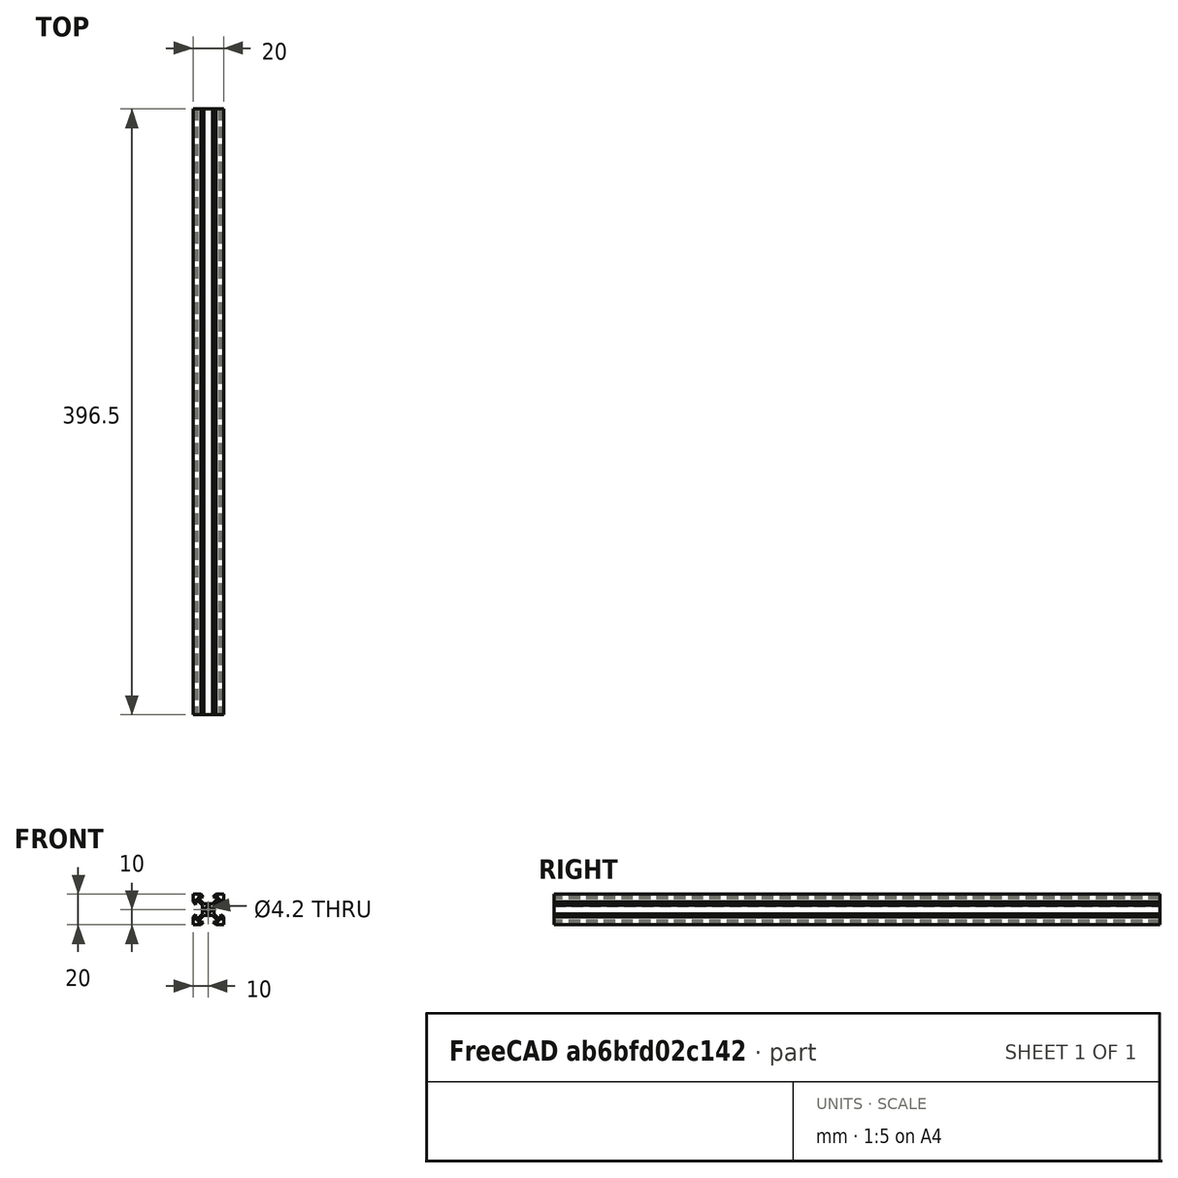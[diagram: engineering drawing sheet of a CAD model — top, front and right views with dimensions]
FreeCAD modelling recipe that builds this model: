
FCSTD DOCUMENT  (FreeCAD 0.20R29177 (Git))
Label: Vlot short
License: All rights reserved
LicenseURL: http://en.wikipedia.org/wiki/All_rights_reserved
objects: Sketcher::SketchObject×1, PartDesign::Pad×1, PartDesign::Body×1
note: 4 computed .brp shape members not serialized (recipe doc carries the construction recipe); baked Part::Feature solids carry a one-line shape summary decoded from their .brp

FEATURE [Sketcher::SketchObject] Sketch
  FullyConstrained = true
  MapMode = 5
  Placement = pos=(0,0,0) rot=(1,0,0;1.5708rad)
  Support = -> [XZ_Plane]
  sketch-geometry (43):
    g0: LineSegment StartX=0 StartY=0 StartZ=0 EndX=5.05 EndY=0 EndZ=0
    g1: LineSegment StartX=20 StartY=20 StartZ=0 EndX=14.95 EndY=20 EndZ=0
    g2: LineSegment StartX=0 StartY=20 StartZ=0 EndX=0 EndY=14.95 EndZ=0
    g3: LineSegment StartX=5.05 StartY=20 StartZ=0 EndX=6.9 EndY=18.15 EndZ=0
    g4: LineSegment StartX=6.9 StartY=18.15 StartZ=0 EndX=2.91066 EndY=18.15 EndZ=0
    g5: LineSegment StartX=2.91066 StartY=18.15 StartZ=0 EndX=7.16066 EndY=13.9 EndZ=0
    g6: LineSegment StartX=7.16066 StartY=13.9 StartZ=0 EndX=12.8393 EndY=13.9 EndZ=0
    g7: LineSegment StartX=12.8393 StartY=13.9 StartZ=0 EndX=17.0893 EndY=18.15 EndZ=0
    g8: LineSegment StartX=17.0893 StartY=18.15 StartZ=0 EndX=13.1 EndY=18.15 EndZ=0
    g9: LineSegment StartX=13.1 StartY=18.15 StartZ=0 EndX=14.95 EndY=20 EndZ=0
    g10: LineSegment StartX=0 StartY=20 StartZ=0 EndX=2.91066 EndY=18.15 EndZ=0
    g11: LineSegment StartX=17.0893 StartY=18.15 StartZ=0 EndX=20 EndY=20 EndZ=0
    g12: LineSegment StartX=0 StartY=20 StartZ=0 EndX=20 EndY=0 EndZ=0
    g13: LineSegment StartX=5.05 StartY=20 StartZ=0 EndX=0 EndY=20 EndZ=0
    g14: LineSegment StartX=0 StartY=20 StartZ=0 EndX=20 EndY=20 EndZ=0
    g15: LineSegment StartX=20 StartY=14.95 StartZ=0 EndX=18.15 EndY=13.1 EndZ=0
    g16: LineSegment StartX=18.15 StartY=13.1 StartZ=0 EndX=18.15 EndY=17.0893 EndZ=0
    g17: LineSegment StartX=18.15 StartY=17.0893 StartZ=0 EndX=13.9 EndY=12.8393 EndZ=0
    g18: LineSegment StartX=13.9 StartY=12.8393 StartZ=0 EndX=13.9 EndY=7.16066 EndZ=0
    g19: LineSegment StartX=13.9 StartY=7.16066 StartZ=0 EndX=18.15 EndY=2.91066 EndZ=0
    g20: LineSegment StartX=20 StartY=14.95 StartZ=0 EndX=20 EndY=20 EndZ=0
    g21: LineSegment StartX=18.15 StartY=2.91066 StartZ=0 EndX=18.15 EndY=6.9 EndZ=0
    g22: LineSegment StartX=18.15 StartY=6.9 StartZ=0 EndX=20 EndY=5.05 EndZ=0
    g23: LineSegment StartX=20 StartY=5.05 StartZ=0 EndX=20 EndY=0 EndZ=0
    g24: LineSegment StartX=5.05 StartY=0 StartZ=0 EndX=6.9 EndY=1.85 EndZ=0
    g25: LineSegment StartX=6.9 StartY=1.85 StartZ=0 EndX=2.91066 EndY=1.85 EndZ=0
    g26: LineSegment StartX=2.91066 StartY=1.85 StartZ=0 EndX=7.16066 EndY=6.1 EndZ=0
    g27: LineSegment StartX=7.16066 StartY=6.1 StartZ=0 EndX=12.8393 EndY=6.1 EndZ=0
    g28: LineSegment StartX=12.8393 StartY=6.1 StartZ=0 EndX=17.0893 EndY=1.85 EndZ=0
    g29: LineSegment StartX=17.0893 StartY=1.85 StartZ=0 EndX=13.1 EndY=1.85 EndZ=0
    g30: LineSegment StartX=13.1 StartY=1.85 StartZ=0 EndX=14.95 EndY=0 EndZ=0
    g31: LineSegment StartX=14.95 StartY=0 StartZ=0 EndX=20 EndY=0 EndZ=0
    g32: LineSegment StartX=0 StartY=14.95 StartZ=0 EndX=1.85 EndY=13.1 EndZ=0
    g33: LineSegment StartX=1.85 StartY=13.1 StartZ=0 EndX=1.85 EndY=17.0893 EndZ=0
    g34: LineSegment StartX=1.85 StartY=17.0893 StartZ=0 EndX=6.1 EndY=12.8393 EndZ=0
    g35: LineSegment StartX=6.1 StartY=12.8393 StartZ=0 EndX=6.1 EndY=7.16066 EndZ=0
    g36: LineSegment StartX=6.1 StartY=7.16066 StartZ=0 EndX=1.85 EndY=2.91066 EndZ=0
    g37: LineSegment StartX=1.85 StartY=2.91066 StartZ=0 EndX=1.85 EndY=6.9 EndZ=0
    g38: LineSegment StartX=1.85 StartY=6.9 StartZ=0 EndX=-2e-16 EndY=5.05 EndZ=0
    g39: LineSegment StartX=-2e-16 StartY=5.05 StartZ=0 EndX=0 EndY=0 EndZ=0
    g40: LineSegment StartX=0 StartY=20 StartZ=0 EndX=0 EndY=0 EndZ=0
    g41: LineSegment StartX=0 StartY=0 StartZ=0 EndX=10 EndY=10 EndZ=0
    g42: Circle CenterX=10 CenterY=10 CenterZ=0 NormalX=0 NormalY=0 NormalZ=1 AngleXU=0 Radius=2.1
  constraints (119):
    c: Coincident(g20,g1)
    c: Coincident(g13,g2)
    c: Coincident(g39,g0)
    c: Horizontal(g0)
    c: Horizontal(g1)
    c: Vertical(g2)
    c: Coincident(g0,g-1)
    c: DistanceY(g39,g2) = 20
    c: Coincident(g4,g3)
    c: Horizontal(g4)
    c: Coincident(g6,g5)
    c: Horizontal(g6)
    c: Coincident(g8,g7)
    c: Horizontal(g8)
    c: Coincident(g9,g8)
    c: Equal(g3,g9)
    c: Equal(g8,g4)
    c: Equal(g5,g7)
    c: Coincident(g4,g5)
    c: PointOnObject(g3,g8)
    c: Coincident(g7,g6)
    c: Coincident(g10,g13)
    c: Coincident(g10,g4)
    c: Coincident(g11,g7)
    c: Coincident(g11,g20)
    c: Equal(g10,g11)
    c: Coincident(g12,g13)
    c: Coincident(g12,g31)
    c: Parallel(g5,g12)
    c: Parallel(g3,g5)
    c: DistanceY(g3,g3) = 1.85
    c: DistanceY(g5,g3) = 6.1
    c: DistanceX(g3,g8) = 6.2
    c: Distance(g5,g12) = 0.75
    c: Coincident(g1,g9)
    c: Coincident(g13,g3)
    c: Tangent(g1,g13)
    c: Coincident(g14,g2)
    c: Coincident(g14,g20)
    c: Coincident(g16,g15)
    c: Coincident(g17,g16)
    c: Coincident(g18,g17)
    c: Vertical(g18)
    c: Coincident(g19,g18)
    c: Coincident(g20,g15)
    c: Equal(g9,g15)
    c: Vertical(g16)
    c: Equal(g17,g19)
    c: Parallel(g7,g17)
    c: Parallel(g17,g15)
    c: Parallel(g19,g12)
    c: Equal(g17,g7)
    c: Equal(g18,g6)
    c: Vertical(g20)
    c: Equal(g16,g8)
    c: Equal(g1,g20)
    c: Coincident(g21,g19)
    c: Vertical(g21)
    c: Coincident(g22,g21)
    c: Coincident(g23,g22)
    c: Coincident(g23,g31)
    c: Equal(g16,g21)
    c: Equal(g22,g15)
    c: Equal(g23,g20)
    c: Coincident(g25,g24)
    c: Horizontal(g25)
    c: Coincident(g26,g25)
    c: Horizontal(g27)
    c: Coincident(g29,g28)
    c: Horizontal(g29)
    c: Coincident(g30,g29)
    c: Equal(g24,g30)
    c: Equal(g29,g25)
    c: Equal(g26,g28)
    c: Coincident(g28,g27)
    c: Coincident(g27,g26)
    c: Parallel(g28,g12)
    c: Parallel(g24,g26)
    c: Parallel(g26,g17)
    c: Equal(g30,g22)
    c: Equal(g28,g19)
    c: Equal(g27,g18)
    c: Equal(g29,g21)
    c: Coincident(g0,g24)
    c: Coincident(g31,g30)
    c: Tangent(g0,g31)
    c: Vertical(g23)
    c: Equal(g23,g31)
    c: Coincident(g33,g32)
    c: Vertical(g33)
    c: Coincident(g34,g33)
    c: Coincident(g35,g34)
    c: Vertical(g35)
    c: Coincident(g36,g35)
    c: Coincident(g37,g36)
    c: Vertical(g37)
    c: Coincident(g38,g37)
    c: Coincident(g2,g32)
    c: Coincident(g39,g38)
    c: Tangent(g2,g39)
    c: Equal(g32,g38)
    c: Equal(g36,g34)
    c: Equal(g35,g27)
    c: Equal(g26,g36)
    c: Equal(g38,g24)
    c: Equal(g0,g39)
    c: Parallel(g38,g36)
    c: Parallel(g38,g26)
    c: Parallel(g34,g32)
    c: Equal(g2,g13)
    c: Equal(g33,g4)
    c: Coincident(g40,g2)
    c: Coincident(g40,g0)
    c: Equal(g14,g40)
    c: Coincident(g41,g0)
    c: PointOnObject(g41,g12)
    c: Perpendicular(g12,g41)
    c: Coincident(g42,g41)
    c: Diameter(g42) = 4.2
FEATURE [PartDesign::Pad] Pad
  Direction = (1,1,1)
  Length = 396.5
  Length2 = 100
  Placement = pos=(0,0,0) rot=(1,0,0;1.5708rad)
  Profile = -> Sketch
  Type = 0
FEATURE [PartDesign::Body] Body  label="Vslot 1"
  Group = -> [Sketch,Pad]
  Origin = -> Origin
  Tip = -> Pad
